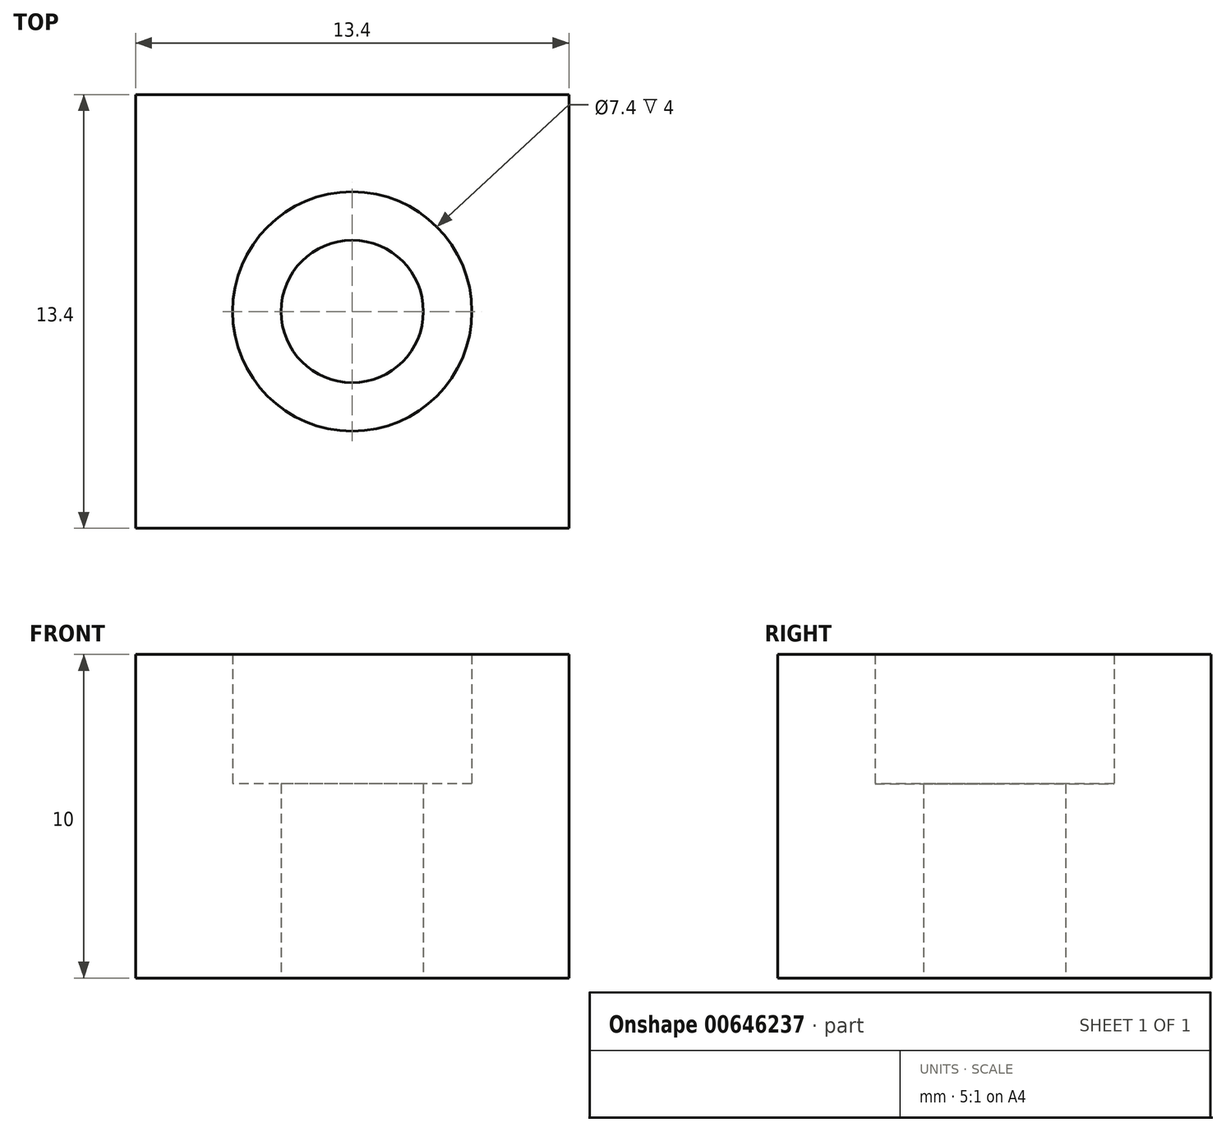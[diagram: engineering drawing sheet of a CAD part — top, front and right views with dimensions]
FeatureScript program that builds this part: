
annotation { "Feature Type Name" : "Feature", "Feature Type Description" : "" }
export const myFeature = defineFeature(function(context is Context, id is Id, definition is map)
    precondition{}
    {
        {
            var Q0;
            Q0=qCreatedBy(makeId("Top.planeOp"),FACE);
            var sketch = newSketch(context, id + "F0", { "sketchPlane" : qUnion([Q0])});
            skCircle(sketch, "E0", {"center": v(0, 0) * mm, "radius": 2.2 * mm});
            skLineSegment(sketch, "E1.bottom", {"start": v(6.7, 6.7) * mm, "end": v(-6.7, 6.7) * mm});
            skLineSegment(sketch, "E1.top", {"start": v(6.7, -6.7) * mm, "end": v(-6.7, -6.7) * mm});
            skLineSegment(sketch, "E1.left", {"start": v(6.7, 6.7) * mm, "end": v(6.7, -6.7) * mm});
            skLineSegment(sketch, "E1.right", {"start": v(-6.7, 6.7) * mm, "end": v(-6.7, -6.7) * mm});
            skSolve(sketch);
        }
        {
            var Q0;
            Q0=makeQuery(id+"F0.imprint","IMPRINT",FACE,{"disambiguationData":[TD([[makeQuery(id+"F0.imprint","IMPRINT",EDGE,{"derivedFrom":sQuery(id+"F0.wireOp",EDGE,"E0")}),-1.0]])]});
            extrude(context, id + "F1", {"entities" : qUnion([Q0]), "depth" : 6 * mm, "offsetDistance" : 25 * mm});
        }
        {
            var Q0;
            Q0=makeQuery(id+"F1.opExtrude","CAP_FACE",FACE,{"disambiguationData":[OSD([sQuery(id+"F0.wireOp",EDGE,"E0"),sQuery(id+"F0.wireOp",EDGE,"E1.bottom"),sQuery(id+"F0.wireOp",EDGE,"E1.top"),sQuery(id+"F0.wireOp",EDGE,"E1.left"),sQuery(id+"F0.wireOp",EDGE,"E1.right")])],"isStart":false});
            var sketch = newSketch(context, id + "F2", { "sketchPlane" : qUnion([Q0])});
            skPoint(sketch, "E2.0", {"position": v(0, 0) * mm});
            skLineSegment(sketch, "E3.bottom", {"start": v(6.7, 6.7) * mm, "end": v(-6.7, 6.7) * mm});
            skLineSegment(sketch, "E3.top", {"start": v(6.7, -6.7) * mm, "end": v(-6.7, -6.7) * mm});
            skLineSegment(sketch, "E3.left", {"start": v(6.7, 6.7) * mm, "end": v(6.7, -6.7) * mm});
            skLineSegment(sketch, "E3.right", {"start": v(-6.7, 6.7) * mm, "end": v(-6.7, -6.7) * mm});
            skCircle(sketch, "E4", {"center": v(0, 0) * mm, "radius": 3.7 * mm});
            skSolve(sketch);
        }
        {
            var Q0;
            Q0=makeQuery(id+"F2.imprint","IMPRINT",FACE,{"disambiguationData":[TD([[makeQuery(id+"F2.imprint","IMPRINT",EDGE,{"derivedFrom":sQuery(id+"F2.wireOp",EDGE,"E3.bottom")}),1.0]])]});
            extrude(context, id + "F3", {"entities" : qUnion([Q0]), "operationType" : NewBodyOperationType.ADD, "depth" : 4 * mm, "offsetDistance" : 25 * mm});
        }
    });
